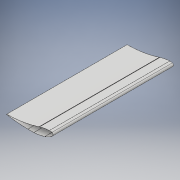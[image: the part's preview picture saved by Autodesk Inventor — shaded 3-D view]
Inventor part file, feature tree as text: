
AUTODESK INVENTOR PART (.ipt)
format: ipt  version: 2018.2 (Build 222227000, 227)  size: 126,976 bytes
history: native  units: mm
features: extrude x1, shell x1, sketch x1, projected_geometry x1
ambient origin geometry x8: Origin, YZ Plane, XZ Plane, XY Plane, X Axis, Y Axis, Z Axis, Center Point
bodies: Body1 (feature_tree)
feature tree (4):
  extrude  "押し出し1"  Depth=946.0mm TaperAngle=0.0deg
  shell  "シェル1"  Thickness=1.0mm
  sketch  "スケッチ1"
  projected_geometry  "投影ループ1"
